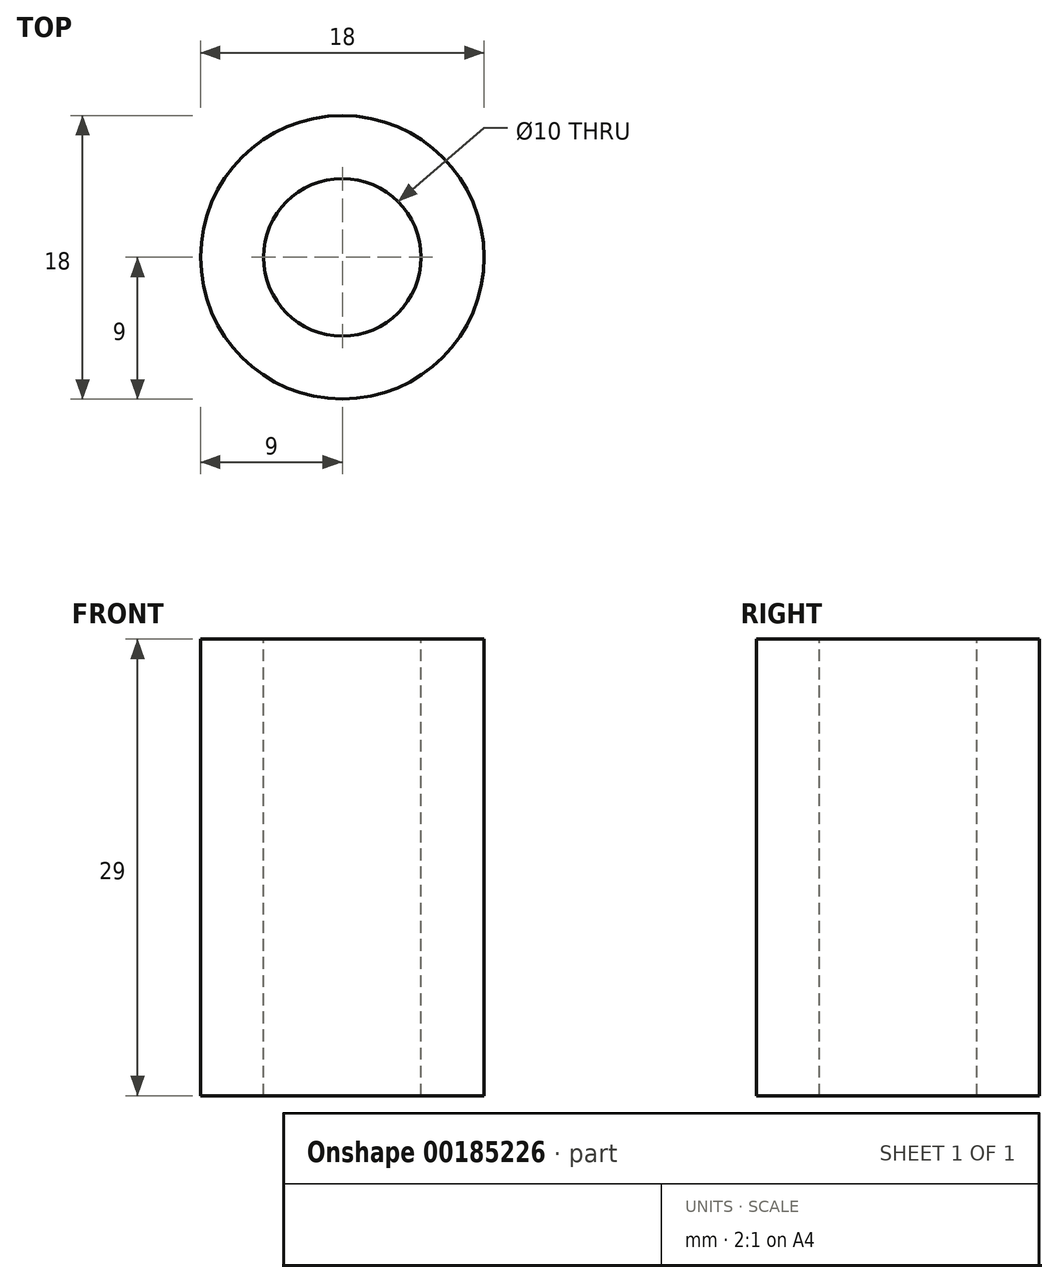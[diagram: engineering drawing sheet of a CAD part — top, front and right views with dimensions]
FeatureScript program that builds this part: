
annotation { "Feature Type Name" : "Feature", "Feature Type Description" : "" }
export const myFeature = defineFeature(function(context is Context, id is Id, definition is map)
    precondition{}
    {
        {
            var Q0;
            Q0=qCreatedBy(makeId("Front.planeOp"),FACE);
            var sketch = newSketch(context, id + "F0", { "sketchPlane" : qUnion([Q0])});
            skLineSegment(sketch, "E0.bottom", {"start": v(9, -14.5) * mm, "end": v(5, -14.5) * mm});
            skLineSegment(sketch, "E0.top", {"start": v(9, 14.5) * mm, "end": v(5, 14.5) * mm});
            skLineSegment(sketch, "E0.left", {"start": v(9, -14.5) * mm, "end": v(9, 14.5) * mm});
            skLineSegment(sketch, "E0.right", {"start": v(5, -14.5) * mm, "end": v(5, 14.5) * mm});
            skPoint(sketch, "E0.middle", {"position": v(7, 0) * mm});
            skLineSegment(sketch, "E1", {"start": v(0, 14.5) * mm, "end": v(0, -14.5) * mm});
            skSolve(sketch);
        }
        {
            var Q0;
            Q0=makeQuery(id+"F0.imprint","IMPRINT",FACE,{"disambiguationData":[TD([[makeQuery(id+"F0.imprint","IMPRINT",EDGE,{"derivedFrom":sQuery(id+"F0.wireOp",EDGE,"E0.bottom")}),-1.0]])]});
            var Q1;
            Q1=sQuery(id+"F0.wireOp",EDGE,"E1");
            revolve(context, id + "F1", {"entities" : qUnion([Q0]), "axis" : qUnion([Q1]), "revolveType" : RevolveType.FULL});
        }
    });
